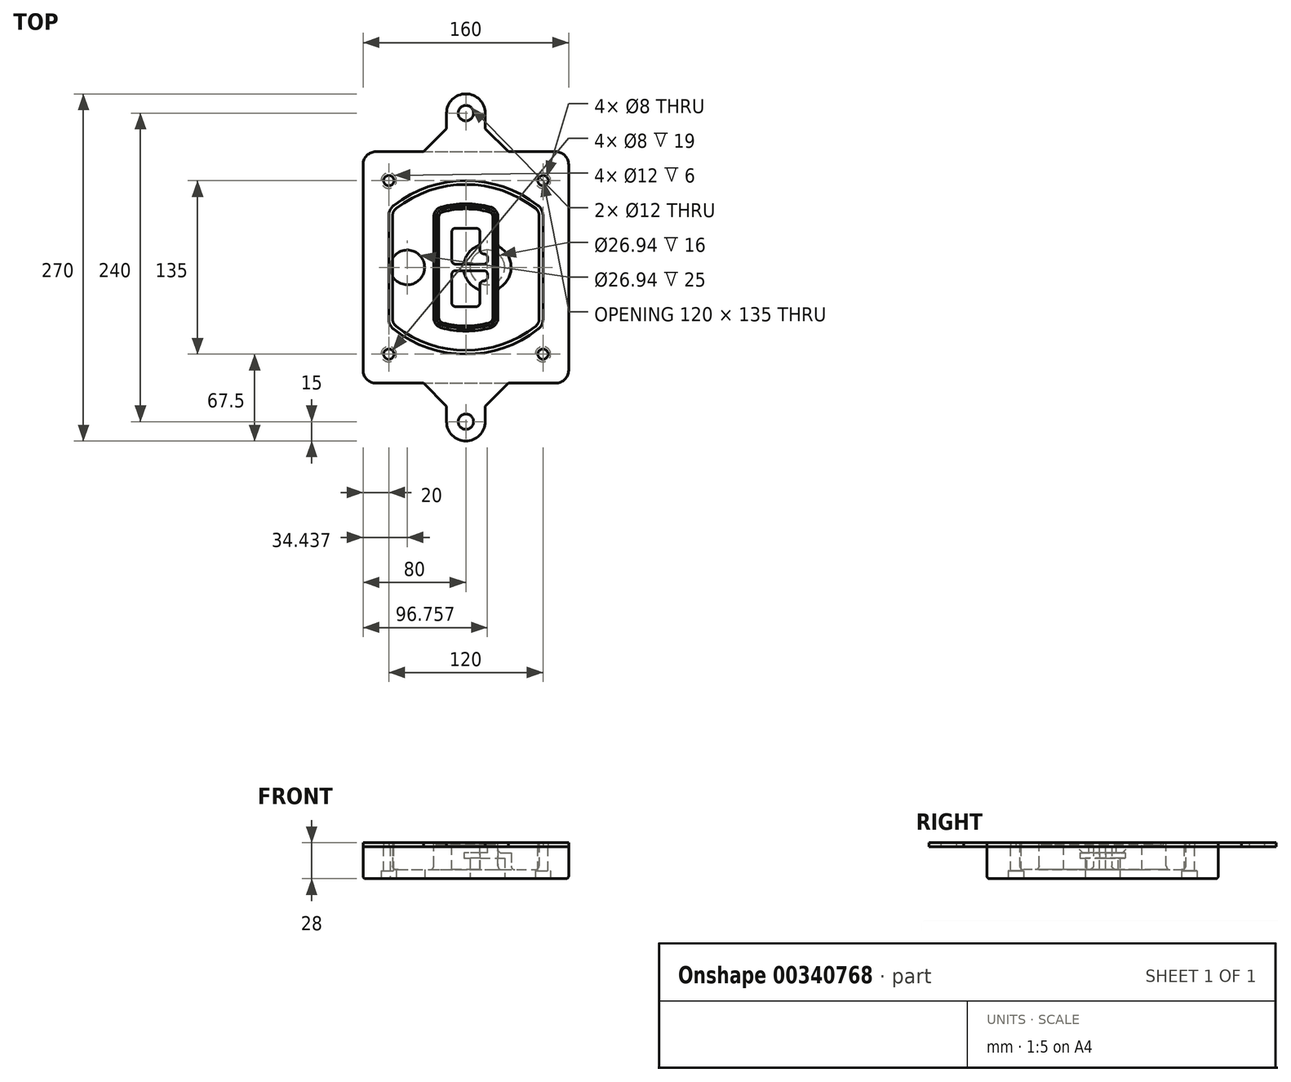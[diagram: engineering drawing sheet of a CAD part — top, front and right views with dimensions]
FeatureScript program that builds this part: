
annotation { "Feature Type Name" : "Feature", "Feature Type Description" : "" }
export const myFeature = defineFeature(function(context is Context, id is Id, definition is map)
    precondition{}
    {
        {
            var Q0;
            Q0=qCreatedBy(makeId("Top.planeOp"),FACE);
            var sketch = newSketch(context, id + "F0", { "sketchPlane" : qUnion([Q0])});
            skPoint(sketch, "E0.rect.middle", {"position": v(0, 0) * mm});
            skLineSegment(sketch, "E1.bottom", {"start": v(-70, -90) * mm, "end": v(70, -90) * mm});
            skLineSegment(sketch, "E1.top", {"start": v(-70, 90) * mm, "end": v(70, 90) * mm});
            skLineSegment(sketch, "E1.left", {"start": v(-80, -80) * mm, "end": v(-80, 80) * mm});
            skLineSegment(sketch, "E1.right", {"start": v(80, -80) * mm, "end": v(80, 80) * mm});
            skLineSegment(sketch, "E2", {"start": v(-80, 90) * mm, "end": v(80, -90) * mm, "construction": true});
            skLineSegment(sketch, "E3", {"start": v(80, 90) * mm, "end": v(-80, -90) * mm, "construction": true});
            skCircle(sketch, "E4", {"center": v(-60, 67.5) * mm, "radius": 4 * mm});
            skCircle(sketch, "E5", {"center": v(60, 67.5) * mm, "radius": 4 * mm});
            skCircle(sketch, "E6", {"center": v(60, -67.5) * mm, "radius": 4 * mm});
            skCircle(sketch, "E7", {"center": v(-60, -67.5) * mm, "radius": 4 * mm});
            skLineSegment(sketch, "E8", {"start": v(-60, 67.5) * mm, "end": v(60, 67.5) * mm, "construction": true});
            skLineSegment(sketch, "E9", {"start": v(60, 67.5) * mm, "end": v(60, -67.5) * mm, "construction": true});
            skLineSegment(sketch, "E10", {"start": v(60, -67.5) * mm, "end": v(-60, -67.5) * mm, "construction": true});
            skLineSegment(sketch, "E11", {"start": v(-60, -67.5) * mm, "end": v(-60, 67.5) * mm, "construction": true});
            skLineSegment(sketch, "E12", {"start": v(-60, 40.3) * mm, "end": v(-60, -40.3) * mm});
            skLineSegment(sketch, "E13", {"start": v(60, 40.3) * mm, "end": v(60, -40.3) * mm});
            skArc(sketch, "E14", {"start": v(56.15, 48.18) * mm, "mid": v(0, 67.5) * mm, "end": v(-56.15, 48.18) * mm});
            skArc(sketch, "E15", {"start": v(-56.15, -48.18) * mm, "mid": v(0, -67.5) * mm, "end": v(56.15, -48.18) * mm});
            skLineSegment(sketch, "E16", {"start": v(-60, 0) * mm, "end": v(60, 0) * mm, "construction": true});
            skPoint(sketch, "E17.visualSharp", {"position": v(-60, -45) * mm});
            skArc(sketch, "E17.filletArc", {"start": v(-60, -40.3) * mm, "mid": v(-58.99, -44.68) * mm, "end": v(-56.15, -48.18) * mm});
            skPoint(sketch, "E18.visualSharp", {"position": v(-60, 45) * mm});
            skArc(sketch, "E18.filletArc", {"start": v(-56.15, 48.18) * mm, "mid": v(-58.99, 44.68) * mm, "end": v(-60, 40.3) * mm});
            skPoint(sketch, "E19.visualSharp", {"position": v(60, 45) * mm});
            skArc(sketch, "E19.filletArc", {"start": v(60, 40.3) * mm, "mid": v(58.99, 44.68) * mm, "end": v(56.15, 48.18) * mm});
            skPoint(sketch, "E20.visualSharp", {"position": v(60, -45) * mm});
            skArc(sketch, "E20.filletArc", {"start": v(56.15, -48.18) * mm, "mid": v(58.99, -44.68) * mm, "end": v(60, -40.3) * mm});
            skPoint(sketch, "E21.visualSharp", {"position": v(-80, 90) * mm});
            skArc(sketch, "E21.filletArc", {"start": v(-70, 90) * mm, "mid": v(-77.07, 87.07) * mm, "end": v(-80, 80) * mm});
            skPoint(sketch, "E22.visualSharp", {"position": v(80, 90) * mm});
            skArc(sketch, "E22.filletArc", {"start": v(80, 80) * mm, "mid": v(77.07, 87.07) * mm, "end": v(70, 90) * mm});
            skPoint(sketch, "E23.visualSharp", {"position": v(80, -90) * mm});
            skArc(sketch, "E23.filletArc", {"start": v(70, -90) * mm, "mid": v(77.07, -87.07) * mm, "end": v(80, -80) * mm});
            skPoint(sketch, "E24.visualSharp", {"position": v(-80, -90) * mm});
            skArc(sketch, "E24.filletArc", {"start": v(-80, -80) * mm, "mid": v(-77.07, -87.07) * mm, "end": v(-70, -90) * mm});
            skArc(sketch, "E25.0", {"start": v(57, 40.3) * mm, "mid": v(56.3, 43.36) * mm, "end": v(54.3, 45.81) * mm});
            skLineSegment(sketch, "E25.1", {"start": v(57, 40.3) * mm, "end": v(57, -40.3) * mm});
            skArc(sketch, "E25.2", {"start": v(54.3, -45.81) * mm, "mid": v(56.3, -43.36) * mm, "end": v(57, -40.3) * mm});
            skArc(sketch, "E25.3", {"start": v(-54.3, -45.81) * mm, "mid": v(0, -64.5) * mm, "end": v(54.3, -45.81) * mm});
            skArc(sketch, "E25.4", {"start": v(-57, -40.3) * mm, "mid": v(-56.3, -43.36) * mm, "end": v(-54.3, -45.81) * mm});
            skArc(sketch, "E25.5", {"start": v(54.3, 45.81) * mm, "mid": v(0, 64.5) * mm, "end": v(-54.3, 45.81) * mm});
            skLineSegment(sketch, "E25.6", {"start": v(-57, 40.3) * mm, "end": v(-57, -40.3) * mm});
            skArc(sketch, "E25.7", {"start": v(-54.3, 45.81) * mm, "mid": v(-56.3, 43.36) * mm, "end": v(-57, 40.3) * mm});
            skArc(sketch, "E26.0", {"start": v(-58.62, 51.33) * mm, "mid": v(-62.58, 46.43) * mm, "end": v(-64, 40.3) * mm});
            skArc(sketch, "E26.1", {"start": v(58.62, 51.33) * mm, "mid": v(0, 71.5) * mm, "end": v(-58.62, 51.33) * mm});
            skArc(sketch, "E26.2", {"start": v(64, 40.3) * mm, "mid": v(62.58, 46.43) * mm, "end": v(58.62, 51.33) * mm});
            skLineSegment(sketch, "E26.3", {"start": v(64, 40.3) * mm, "end": v(64, -40.3) * mm});
            skArc(sketch, "E26.4", {"start": v(58.62, -51.33) * mm, "mid": v(62.58, -46.43) * mm, "end": v(64, -40.3) * mm});
            skLineSegment(sketch, "E26.5", {"start": v(-64, 40.3) * mm, "end": v(-64, -40.3) * mm});
            skArc(sketch, "E26.6", {"start": v(-58.62, -51.33) * mm, "mid": v(0, -71.5) * mm, "end": v(58.62, -51.33) * mm});
            skArc(sketch, "E26.7", {"start": v(-64, -40.3) * mm, "mid": v(-62.58, -46.43) * mm, "end": v(-58.62, -51.33) * mm});
            skSolve(sketch);
        }
        {
            var Q0;
            Q0=makeQuery(id+"F0.imprint","IMPRINT",FACE,{"disambiguationData":[TD([[makeQuery(id+"F0.imprint","IMPRINT",EDGE,{"derivedFrom":sQuery(id+"F0.wireOp",EDGE,"E1.bottom")}),1.0]])]});
            var Q1;
            Q1=makeQuery(id+"F0.imprint","IMPRINT",FACE,{"disambiguationData":[TD([[makeQuery(id+"F0.imprint","IMPRINT",EDGE,{"derivedFrom":sQuery(id+"F0.wireOp",EDGE,"E12")}),1.0]])]});
            var Q2;
            Q2=makeQuery(id+"F0.imprint","IMPRINT",FACE,{"disambiguationData":[TD([[makeQuery(id+"F0.imprint","IMPRINT",EDGE,{"derivedFrom":sQuery(id+"F0.wireOp",EDGE,"E25.0")}),1.0]])]});
            var Q3;
            Q3=makeQuery(id+"F0.imprint","IMPRINT",FACE,{"disambiguationData":[TD([[makeQuery(id+"F0.imprint","IMPRINT",EDGE,{"derivedFrom":sQuery(id+"F0.wireOp",EDGE,"E12")}),-1.0]])]});
            extrude(context, id + "F1", {"entities" : qUnion([Q0, Q1, Q2, Q3]), "oppositeDirection" : true, "depth" : 25 * mm});
        }
        {
            var Q0;
            Q0=makeQuery(id+"F0.imprint","IMPRINT",FACE,{"disambiguationData":[TD([[makeQuery(id+"F0.imprint","IMPRINT",EDGE,{"derivedFrom":sQuery(id+"F0.wireOp",EDGE,"E12")}),1.0]])]});
            extrude(context, id + "F2", {"entities" : qUnion([Q0]), "operationType" : NewBodyOperationType.ADD, "depth" : 3 * mm});
        }
        {
            var Q0;
            Q0=makeQuery(id+"F0.imprint","IMPRINT",FACE,{"disambiguationData":[TD([[makeQuery(id+"F0.imprint","IMPRINT",EDGE,{"derivedFrom":sQuery(id+"F0.wireOp",EDGE,"E25.0")}),1.0]])]});
            extrude(context, id + "F3", {"entities" : qUnion([Q0]), "operationType" : NewBodyOperationType.REMOVE, "oppositeDirection" : true, "depth" : 18 * mm});
        }
        {
            var Q0;
            Q0=makeQuery(id+"F2.opExtrude","CAP_FACE",FACE,{"disambiguationData":[OSD([sQuery(id+"F0.wireOp",EDGE,"E12"),sQuery(id+"F0.wireOp",EDGE,"E13"),sQuery(id+"F0.wireOp",EDGE,"E14"),sQuery(id+"F0.wireOp",EDGE,"E15"),sQuery(id+"F0.wireOp",EDGE,"E17.filletArc"),sQuery(id+"F0.wireOp",EDGE,"E18.filletArc"),sQuery(id+"F0.wireOp",EDGE,"E19.filletArc"),sQuery(id+"F0.wireOp",EDGE,"E20.filletArc"),sQuery(id+"F0.wireOp",EDGE,"E25.0"),sQuery(id+"F0.wireOp",EDGE,"E25.1"),sQuery(id+"F0.wireOp",EDGE,"E25.2"),sQuery(id+"F0.wireOp",EDGE,"E25.3"),sQuery(id+"F0.wireOp",EDGE,"E25.4"),sQuery(id+"F0.wireOp",EDGE,"E25.5"),sQuery(id+"F0.wireOp",EDGE,"E25.6"),sQuery(id+"F0.wireOp",EDGE,"E25.7")])],"isStart":false});
            var sketch = newSketch(context, id + "F4", { "sketchPlane" : qUnion([Q0])});
            skArc(sketch, "E27.0", {"start": v(-19.08, -46.97) * mm, "mid": v(0, -49.5) * mm, "end": v(19.08, -46.97) * mm});
            skArc(sketch, "E28.0", {"start": v(19.08, 46.97) * mm, "mid": v(0, 49.5) * mm, "end": v(-19.08, 46.97) * mm});
            skLineSegment(sketch, "E29", {"start": v(-25, 39.25) * mm, "end": v(-25, -39.25) * mm});
            skLineSegment(sketch, "E30", {"start": v(25, 39.25) * mm, "end": v(25, -39.25) * mm});
            skLineSegment(sketch, "E31", {"start": v(-25, 45.1) * mm, "end": v(25, 45.1) * mm, "construction": true});
            skLineSegment(sketch, "E32", {"start": v(-25, -45.1) * mm, "end": v(25, -45.1) * mm, "construction": true});
            skPoint(sketch, "E33.visualSharp", {"position": v(-25, 45.1) * mm});
            skArc(sketch, "E33.filletArc", {"start": v(-19.08, 46.97) * mm, "mid": v(-23.35, 44.11) * mm, "end": v(-25, 39.25) * mm});
            skPoint(sketch, "E34.visualSharp", {"position": v(25, 45.1) * mm});
            skArc(sketch, "E34.filletArc", {"start": v(25, 39.25) * mm, "mid": v(23.35, 44.11) * mm, "end": v(19.08, 46.97) * mm});
            skPoint(sketch, "E35.visualSharp", {"position": v(25, -45.1) * mm});
            skArc(sketch, "E35.filletArc", {"start": v(19.08, -46.97) * mm, "mid": v(23.35, -44.11) * mm, "end": v(25, -39.25) * mm});
            skPoint(sketch, "E36.visualSharp", {"position": v(-25, -45.1) * mm});
            skArc(sketch, "E36.filletArc", {"start": v(-25, -39.25) * mm, "mid": v(-23.35, -44.11) * mm, "end": v(-19.08, -46.97) * mm});
            skArc(sketch, "E37.0", {"start": v(54.3, 45.81) * mm, "mid": v(0, 64.5) * mm, "end": v(-54.3, 45.81) * mm});
            skArc(sketch, "E37.1", {"start": v(-54.3, 45.81) * mm, "mid": v(-56.3, 43.36) * mm, "end": v(-57, 40.3) * mm});
            skLineSegment(sketch, "E37.2", {"start": v(-57, 40.3) * mm, "end": v(-57, -40.3) * mm});
            skArc(sketch, "E37.3", {"start": v(-57, -40.3) * mm, "mid": v(-56.3, -43.36) * mm, "end": v(-54.3, -45.81) * mm});
            skArc(sketch, "E37.4", {"start": v(-54.3, -45.81) * mm, "mid": v(0, -64.5) * mm, "end": v(54.3, -45.81) * mm});
            skArc(sketch, "E37.5", {"start": v(54.3, -45.81) * mm, "mid": v(56.3, -43.36) * mm, "end": v(57, -40.3) * mm});
            skLineSegment(sketch, "E37.6", {"start": v(57, 40.3) * mm, "end": v(57, -40.3) * mm});
            skArc(sketch, "E37.7", {"start": v(57, 40.3) * mm, "mid": v(56.3, 43.36) * mm, "end": v(54.3, 45.81) * mm});
            skLineSegment(sketch, "E38.0", {"start": v(23, 39.25) * mm, "end": v(23, -39.25) * mm});
            skArc(sketch, "E38.1", {"start": v(18.56, -45.04) * mm, "mid": v(21.76, -42.9) * mm, "end": v(23, -39.25) * mm});
            skArc(sketch, "E38.2", {"start": v(-18.56, -45.04) * mm, "mid": v(0, -47.5) * mm, "end": v(18.56, -45.04) * mm});
            skArc(sketch, "E38.3", {"start": v(-23, -39.25) * mm, "mid": v(-21.76, -42.9) * mm, "end": v(-18.56, -45.04) * mm});
            skLineSegment(sketch, "E38.4", {"start": v(-23, 39.25) * mm, "end": v(-23, -39.25) * mm});
            skArc(sketch, "E38.5", {"start": v(23, 39.25) * mm, "mid": v(21.76, 42.9) * mm, "end": v(18.56, 45.04) * mm});
            skArc(sketch, "E38.6", {"start": v(-18.56, 45.04) * mm, "mid": v(-21.76, 42.9) * mm, "end": v(-23, 39.25) * mm});
            skArc(sketch, "E38.7", {"start": v(18.56, 45.04) * mm, "mid": v(0, 47.5) * mm, "end": v(-18.56, 45.04) * mm});
            skArc(sketch, "E39.0", {"start": v(21, 39.25) * mm, "mid": v(20.18, 41.68) * mm, "end": v(18.04, 43.1) * mm});
            skLineSegment(sketch, "E39.1", {"start": v(21, 39.25) * mm, "end": v(21, -39.25) * mm});
            skArc(sketch, "E39.2", {"start": v(18.04, -43.1) * mm, "mid": v(20.18, -41.68) * mm, "end": v(21, -39.25) * mm});
            skArc(sketch, "E39.3", {"start": v(-18.04, -43.1) * mm, "mid": v(0, -45.5) * mm, "end": v(18.04, -43.1) * mm});
            skArc(sketch, "E39.4", {"start": v(-21, -39.25) * mm, "mid": v(-20.18, -41.68) * mm, "end": v(-18.04, -43.1) * mm});
            skArc(sketch, "E39.5", {"start": v(18.04, 43.1) * mm, "mid": v(0, 45.5) * mm, "end": v(-18.04, 43.1) * mm});
            skLineSegment(sketch, "E39.6", {"start": v(-21, 39.25) * mm, "end": v(-21, -39.25) * mm});
            skArc(sketch, "E39.7", {"start": v(-18.04, 43.1) * mm, "mid": v(-20.18, 41.68) * mm, "end": v(-21, 39.25) * mm});
            skLineSegment(sketch, "E40", {"start": v(-25, 0) * mm, "end": v(25, 0) * mm, "construction": true});
            skLineSegment(sketch, "E41", {"start": v(-11, 5.5) * mm, "end": v(-11, 27.5) * mm});
            skLineSegment(sketch, "E42", {"start": v(-8, 30.5) * mm, "end": v(8, 30.5) * mm});
            skLineSegment(sketch, "E43", {"start": v(11, 27.5) * mm, "end": v(11, 13.5) * mm});
            skLineSegment(sketch, "E44", {"start": v(14, 10.5) * mm, "end": v(14, 10.5) * mm});
            skLineSegment(sketch, "E45", {"start": v(17, 7.5) * mm, "end": v(17, 5.5) * mm});
            skLineSegment(sketch, "E46", {"start": v(14, 2.5) * mm, "end": v(-8, 2.5) * mm});
            skPoint(sketch, "E47.visualSharp", {"position": v(-11, 30.5) * mm});
            skArc(sketch, "E47.filletArc", {"start": v(-8, 30.5) * mm, "mid": v(-10.12, 29.62) * mm, "end": v(-11, 27.5) * mm});
            skPoint(sketch, "E48.visualSharp", {"position": v(11, 30.5) * mm});
            skArc(sketch, "E48.filletArc", {"start": v(11, 27.5) * mm, "mid": v(10.12, 29.62) * mm, "end": v(8, 30.5) * mm});
            skPoint(sketch, "E49.visualSharp", {"position": v(11, 10.5) * mm});
            skArc(sketch, "E49.filletArc", {"start": v(11, 13.5) * mm, "mid": v(11.88, 11.38) * mm, "end": v(14, 10.5) * mm});
            skPoint(sketch, "E50.visualSharp", {"position": v(17, 10.5) * mm});
            skArc(sketch, "E50.filletArc", {"start": v(17, 7.5) * mm, "mid": v(16.12, 9.62) * mm, "end": v(14, 10.5) * mm});
            skPoint(sketch, "E51.visualSharp", {"position": v(17, 2.5) * mm});
            skArc(sketch, "E51.filletArc", {"start": v(14, 2.5) * mm, "mid": v(16.12, 3.38) * mm, "end": v(17, 5.5) * mm});
            skPoint(sketch, "E52.visualSharp", {"position": v(-11, 2.5) * mm});
            skArc(sketch, "E52.filletArc", {"start": v(-11, 5.5) * mm, "mid": v(-10.12, 3.38) * mm, "end": v(-8, 2.5) * mm});
            skLineSegment(sketch, "E53.0.MirrorCS", {"start": v(14, -2.5) * mm, "end": v(-8, -2.5) * mm});
            skArc(sketch, "E54.0.MirrorCS", {"start": v(-11, -5.5) * mm, "mid": v(-10.12, -3.38) * mm, "end": v(-8, -2.5) * mm});
            skLineSegment(sketch, "E55.0.MirrorCS", {"start": v(-11, -5.5) * mm, "end": v(-11, -27.5) * mm});
            skArc(sketch, "E56.0.MirrorCS", {"start": v(-8, -30.5) * mm, "mid": v(-10.12, -29.62) * mm, "end": v(-11, -27.5) * mm});
            skLineSegment(sketch, "E57.0.MirrorCS", {"start": v(-8, -30.5) * mm, "end": v(8, -30.5) * mm});
            skArc(sketch, "E58.0.MirrorCS", {"start": v(11, -27.5) * mm, "mid": v(10.12, -29.62) * mm, "end": v(8, -30.5) * mm});
            skLineSegment(sketch, "E59.0.MirrorCS", {"start": v(11, -27.5) * mm, "end": v(11, -13.5) * mm});
            skArc(sketch, "E60.0.MirrorCS", {"start": v(11, -13.5) * mm, "mid": v(11.88, -11.38) * mm, "end": v(14, -10.5) * mm});
            skArc(sketch, "E61.0.MirrorCS", {"start": v(17, -7.5) * mm, "mid": v(16.12, -9.62) * mm, "end": v(14, -10.5) * mm});
            skLineSegment(sketch, "E62.0.MirrorCS", {"start": v(17, -7.5) * mm, "end": v(17, -5.5) * mm});
            skArc(sketch, "E63.0.MirrorCS", {"start": v(14, -2.5) * mm, "mid": v(16.12, -3.38) * mm, "end": v(17, -5.5) * mm});
            skSolve(sketch);
        }
        {
            var Q0;
            Q0=makeQuery(id+"F4.imprint","IMPRINT",FACE,{"disambiguationData":[TD([[makeQuery(id+"F4.imprint","IMPRINT",EDGE,{"derivedFrom":sQuery(id+"F4.wireOp",EDGE,"E27.0")}),1.0]])]});
            var Q1;
            Q1=makeQuery(id+"F4.imprint","IMPRINT",FACE,{"disambiguationData":[TD([[makeQuery(id+"F4.imprint","IMPRINT",EDGE,{"derivedFrom":sQuery(id+"F4.wireOp",EDGE,"E38.0")}),-1.0]])]});
            var Q2;
            Q2=makeQuery(id+"F4.imprint","IMPRINT",FACE,{"disambiguationData":[TD([[makeQuery(id+"F4.imprint","IMPRINT",EDGE,{"derivedFrom":sQuery(id+"F4.wireOp",EDGE,"E39.0")}),1.0]])]});
            extrude(context, id + "F5", {"entities" : qUnion([Q0, Q1, Q2]), "operationType" : NewBodyOperationType.ADD, "endBound" : BoundingType.UP_TO_NEXT, "oppositeDirection" : true, "depth" : 25 * mm});
        }
        {
            var Q0;
            Q0=makeQuery(id+"F4.imprint","IMPRINT",FACE,{"disambiguationData":[TD([[makeQuery(id+"F4.imprint","IMPRINT",EDGE,{"derivedFrom":sQuery(id+"F4.wireOp",EDGE,"E38.0")}),-1.0]])]});
            extrude(context, id + "F6", {"entities" : qUnion([Q0]), "operationType" : NewBodyOperationType.REMOVE, "oppositeDirection" : true, "depth" : 2 * mm});
        }
        {
            var Q0;
            Q0=makeQuery(id+"F1.opExtrude","CAP_FACE",FACE,{"disambiguationData":[OSD([sQuery(id+"F0.wireOp",EDGE,"E1.bottom"),sQuery(id+"F0.wireOp",EDGE,"E1.top"),sQuery(id+"F0.wireOp",EDGE,"E1.left"),sQuery(id+"F0.wireOp",EDGE,"E1.right"),sQuery(id+"F0.wireOp",EDGE,"E4"),sQuery(id+"F0.wireOp",EDGE,"E5"),sQuery(id+"F0.wireOp",EDGE,"E6"),sQuery(id+"F0.wireOp",EDGE,"E7"),sQuery(id+"F0.wireOp",EDGE,"E21.filletArc"),sQuery(id+"F0.wireOp",EDGE,"E22.filletArc"),sQuery(id+"F0.wireOp",EDGE,"E23.filletArc"),sQuery(id+"F0.wireOp",EDGE,"E24.filletArc")])],"isStart":false});
            var sketch = newSketch(context, id + "F7", { "sketchPlane" : qUnion([Q0])});
            skCircle(sketch, "E64", {"center": v(16.76, 0) * mm, "radius": 13.47 * mm});
            skCircle(sketch, "E65", {"center": v(-45.56, 0) * mm, "radius": 13.47 * mm});
            skLineSegment(sketch, "E66", {"start": v(80, 0) * mm, "end": v(-80, 0) * mm});
            skCircle(sketch, "E67", {"center": v(16.76, 0) * mm, "radius": 18.47 * mm});
            skCircle(sketch, "E68", {"center": v(60, -67.5) * mm, "radius": 6 * mm});
            skCircle(sketch, "E69", {"center": v(-60, -67.5) * mm, "radius": 6 * mm});
            skCircle(sketch, "E70", {"center": v(-60, 67.5) * mm, "radius": 6 * mm});
            skCircle(sketch, "E71", {"center": v(60, 67.5) * mm, "radius": 6 * mm});
            skSolve(sketch);
        }
        {
            var Q0;
            {var subQ1=sQuery(id+"F7.wireOp",EDGE,"E66");var subQ4=sQuery(id+"F7.wireOp",EDGE,"E64");var subQ6=makeQuery(id+"F7.imprint","INTERSECT",VERTEX,{"disambiguationData":[OD(0.0)],"derivedFrom":[subQ4,subQ1]});Q0=makeQuery(id+"F7.imprint","IMPRINT",FACE,{"disambiguationData":[TD([[makeQuery(id+"F7.imprint","IMPRINT",EDGE,{"disambiguationData":[TD([[subQ6,-1.0]])],"derivedFrom":subQ4}),-1.0]])]});}
            var Q1;
            {var subQ0=sQuery(id+"F7.wireOp",EDGE,"E66");var subQ1=sQuery(id+"F7.wireOp",EDGE,"E64");var subQ3=makeQuery(id+"F7.imprint","INTERSECT",VERTEX,{"disambiguationData":[OD(0.0)],"derivedFrom":[subQ1,subQ0]});Q1=makeQuery(id+"F7.imprint","IMPRINT",FACE,{"disambiguationData":[TD([[makeQuery(id+"F7.imprint","IMPRINT",EDGE,{"disambiguationData":[TD([[subQ3,-1.0]])],"derivedFrom":subQ1}),1.0]])]});}
            var Q2;
            {var subQ0=sQuery(id+"F7.wireOp",EDGE,"E66");var subQ1=sQuery(id+"F7.wireOp",EDGE,"E64");var subQ3=makeQuery(id+"F7.imprint","INTERSECT",VERTEX,{"disambiguationData":[OD(0.0)],"derivedFrom":[subQ1,subQ0]});Q2=makeQuery(id+"F7.imprint","IMPRINT",FACE,{"disambiguationData":[TD([[makeQuery(id+"F7.imprint","IMPRINT",EDGE,{"disambiguationData":[TD([[subQ3,1.0]])],"derivedFrom":subQ1}),1.0]])]});}
            var Q3;
            {var subQ1=sQuery(id+"F7.wireOp",EDGE,"E66");var subQ4=sQuery(id+"F7.wireOp",EDGE,"E64");var subQ6=makeQuery(id+"F7.imprint","INTERSECT",VERTEX,{"disambiguationData":[OD(0.0)],"derivedFrom":[subQ4,subQ1]});Q3=makeQuery(id+"F7.imprint","IMPRINT",FACE,{"disambiguationData":[TD([[makeQuery(id+"F7.imprint","IMPRINT",EDGE,{"disambiguationData":[TD([[subQ6,1.0]])],"derivedFrom":subQ4}),-1.0]])]});}
            extrude(context, id + "F8", {"entities" : qUnion([Q0, Q1, Q2, Q3]), "operationType" : NewBodyOperationType.ADD, "oppositeDirection" : true, "depth" : 20 * mm});
        }
        {
            var Q0;
            {var subQ0=sQuery(id+"F7.wireOp",EDGE,"E66");var subQ1=sQuery(id+"F7.wireOp",EDGE,"E64");var subQ3=makeQuery(id+"F7.imprint","INTERSECT",VERTEX,{"disambiguationData":[OD(0.0)],"derivedFrom":[subQ1,subQ0]});Q0=makeQuery(id+"F7.imprint","IMPRINT",FACE,{"disambiguationData":[TD([[makeQuery(id+"F7.imprint","IMPRINT",EDGE,{"disambiguationData":[TD([[subQ3,-1.0]])],"derivedFrom":subQ1}),1.0]])]});}
            var Q1;
            {var subQ0=sQuery(id+"F7.wireOp",EDGE,"E66");var subQ1=sQuery(id+"F7.wireOp",EDGE,"E64");var subQ3=makeQuery(id+"F7.imprint","INTERSECT",VERTEX,{"disambiguationData":[OD(0.0)],"derivedFrom":[subQ1,subQ0]});Q1=makeQuery(id+"F7.imprint","IMPRINT",FACE,{"disambiguationData":[TD([[makeQuery(id+"F7.imprint","IMPRINT",EDGE,{"disambiguationData":[TD([[subQ3,1.0]])],"derivedFrom":subQ1}),1.0]])]});}
            extrude(context, id + "F9", {"entities" : qUnion([Q0, Q1]), "operationType" : NewBodyOperationType.REMOVE, "oppositeDirection" : true, "depth" : 16 * mm});
        }
        {
            var Q0;
            {var subQ0=sQuery(id+"F7.wireOp",EDGE,"E66");var subQ1=sQuery(id+"F7.wireOp",EDGE,"E65");var subQ3=makeQuery(id+"F7.imprint","INTERSECT",VERTEX,{"disambiguationData":[OD(0.0)],"derivedFrom":[subQ1,subQ0]});Q0=makeQuery(id+"F7.imprint","IMPRINT",FACE,{"disambiguationData":[TD([[makeQuery(id+"F7.imprint","IMPRINT",EDGE,{"disambiguationData":[TD([[subQ3,-1.0]])],"derivedFrom":subQ1}),1.0]])]});}
            var Q1;
            {var subQ0=sQuery(id+"F7.wireOp",EDGE,"E66");var subQ1=sQuery(id+"F7.wireOp",EDGE,"E65");var subQ3=makeQuery(id+"F7.imprint","INTERSECT",VERTEX,{"disambiguationData":[OD(0.0)],"derivedFrom":[subQ1,subQ0]});Q1=makeQuery(id+"F7.imprint","IMPRINT",FACE,{"disambiguationData":[TD([[makeQuery(id+"F7.imprint","IMPRINT",EDGE,{"disambiguationData":[TD([[subQ3,1.0]])],"derivedFrom":subQ1}),1.0]])]});}
            extrude(context, id + "F10", {"entities" : qUnion([Q0, Q1]), "operationType" : NewBodyOperationType.REMOVE, "oppositeDirection" : true, "depth" : 25 * mm});
        }
        {
            var Q0;
            Q0=makeQuery(id+"F7.imprint","IMPRINT",FACE,{"disambiguationData":[TD([[makeQuery(id+"F7.imprint","IMPRINT",EDGE,{"derivedFrom":sQuery(id+"F7.wireOp",EDGE,"E68")}),1.0]])]});
            var Q1;
            Q1=makeQuery(id+"F7.imprint","IMPRINT",FACE,{"disambiguationData":[TD([[makeQuery(id+"F7.imprint","IMPRINT",EDGE,{"derivedFrom":makeQuery(id+"F1.opExtrude","CAP_EDGE",EDGE,{"disambiguationData":[OSD([sQuery(id+"F0.wireOp",EDGE,"E5")])],"isStart":false})}),-1.0]])]});
            var Q2;
            Q2=makeQuery(id+"F7.imprint","IMPRINT",FACE,{"disambiguationData":[TD([[makeQuery(id+"F7.imprint","IMPRINT",EDGE,{"derivedFrom":sQuery(id+"F7.wireOp",EDGE,"E69")}),1.0]])]});
            var Q3;
            Q3=makeQuery(id+"F7.imprint","IMPRINT",FACE,{"disambiguationData":[TD([[makeQuery(id+"F7.imprint","IMPRINT",EDGE,{"derivedFrom":makeQuery(id+"F1.opExtrude","CAP_EDGE",EDGE,{"disambiguationData":[OSD([sQuery(id+"F0.wireOp",EDGE,"E4")])],"isStart":false})}),-1.0]])]});
            var Q4;
            Q4=makeQuery(id+"F7.imprint","IMPRINT",FACE,{"disambiguationData":[TD([[makeQuery(id+"F7.imprint","IMPRINT",EDGE,{"derivedFrom":sQuery(id+"F7.wireOp",EDGE,"E70")}),1.0]])]});
            var Q5;
            Q5=makeQuery(id+"F7.imprint","IMPRINT",FACE,{"disambiguationData":[TD([[makeQuery(id+"F7.imprint","IMPRINT",EDGE,{"derivedFrom":makeQuery(id+"F1.opExtrude","CAP_EDGE",EDGE,{"disambiguationData":[OSD([sQuery(id+"F0.wireOp",EDGE,"E7")])],"isStart":false})}),-1.0]])]});
            var Q6;
            Q6=makeQuery(id+"F7.imprint","IMPRINT",FACE,{"disambiguationData":[TD([[makeQuery(id+"F7.imprint","IMPRINT",EDGE,{"derivedFrom":sQuery(id+"F7.wireOp",EDGE,"E71")}),1.0]])]});
            var Q7;
            Q7=makeQuery(id+"F7.imprint","IMPRINT",FACE,{"disambiguationData":[TD([[makeQuery(id+"F7.imprint","IMPRINT",EDGE,{"derivedFrom":makeQuery(id+"F1.opExtrude","CAP_EDGE",EDGE,{"disambiguationData":[OSD([sQuery(id+"F0.wireOp",EDGE,"E6")])],"isStart":false})}),-1.0]])]});
            extrude(context, id + "F11", {"entities" : qUnion([Q0, Q1, Q2, Q3, Q4, Q5, Q6, Q7]), "operationType" : NewBodyOperationType.REMOVE, "oppositeDirection" : true, "depth" : 6 * mm});
        }
        {
            var Q0;
            Q0=makeQuery(id+"F9.boolean.opBoolean","COPY",FACE,{"derivedFrom":makeQuery(id+"F9.opExtrude","CAP_FACE",FACE,{"disambiguationData":[OSD([sQuery(id+"F7.wireOp",EDGE,"E64")])],"isStart":false})});
            var sketch = newSketch(context, id + "F12", { "sketchPlane" : qUnion([Q0])});
            skArc(sketch, "E72.0", {"start": v(11, 17.55) * mm, "mid": v(2.57, 11.82) * mm, "end": v(-1.54, 2.5) * mm});
            skArc(sketch, "E72.1", {"start": v(-1.54, -2.5) * mm, "mid": v(2.57, -11.82) * mm, "end": v(11, -17.55) * mm});
            skLineSegment(sketch, "E73", {"start": v(-1.54, -2.5) * mm, "end": v(14, -2.5) * mm});
            skLineSegment(sketch, "E74.0", {"start": v(14, 2.5) * mm, "end": v(-1.54, 2.5) * mm});
            skArc(sketch, "E74.1", {"start": v(14, 2.5) * mm, "mid": v(16.12, 3.38) * mm, "end": v(17, 5.5) * mm});
            skLineSegment(sketch, "E74.2", {"start": v(17, 7.5) * mm, "end": v(17, 5.5) * mm});
            skArc(sketch, "E74.3", {"start": v(17, 7.5) * mm, "mid": v(16.12, 9.62) * mm, "end": v(14, 10.5) * mm});
            skArc(sketch, "E74.4", {"start": v(11, 13.5) * mm, "mid": v(11.88, 11.38) * mm, "end": v(14, 10.5) * mm});
            skLineSegment(sketch, "E74.5", {"start": v(11, 17.55) * mm, "end": v(11, 13.5) * mm});
            skLineSegment(sketch, "E74.7", {"start": v(14, -2.5) * mm, "end": v(-1.54, -2.5) * mm});
            skArc(sketch, "E74.8", {"start": v(14, -2.5) * mm, "mid": v(16.12, -3.38) * mm, "end": v(17, -5.5) * mm});
            skLineSegment(sketch, "E74.9", {"start": v(17, -7.5) * mm, "end": v(17, -5.5) * mm});
            skArc(sketch, "E74.10", {"start": v(17, -7.5) * mm, "mid": v(16.12, -9.62) * mm, "end": v(14, -10.5) * mm});
            skArc(sketch, "E74.11", {"start": v(11, -13.5) * mm, "mid": v(11.88, -11.38) * mm, "end": v(14, -10.5) * mm});
            skLineSegment(sketch, "E74.12", {"start": v(11, -17.55) * mm, "end": v(11, -13.5) * mm});
            skPoint(sketch, "E75.orphan", {"position": v(11, -27.5) * mm});
            skPoint(sketch, "E76.orphan", {"position": v(-8, -2.5) * mm});
            skPoint(sketch, "E77.orphan", {"position": v(-8, 2.5) * mm});
            skPoint(sketch, "E78.orphan", {"position": v(11, 27.5) * mm});
            skSolve(sketch);
        }
        {
            var Q0;
            {var subQ7=sQuery(id+"F12.wireOp",EDGE,"E72.0");var subQ14=sQuery(id+"F12.wireOp",EDGE,"E72.1");var subQ16=sQuery(id+"F12.wireOp",EDGE,"E74.1");var subQ18=sQuery(id+"F12.wireOp",EDGE,"E74.8");Q0=qUnion([makeQuery(id+"F12.imprint","IMPRINT",FACE,{"disambiguationData":[TD([[makeQuery(id+"F12.imprint","IMPRINT",EDGE,{"derivedFrom":subQ7}),1.0]])]}),makeQuery(id+"F12.imprint","IMPRINT",FACE,{"disambiguationData":[TD([[makeQuery(id+"F12.imprint","IMPRINT",EDGE,{"derivedFrom":subQ14}),1.0]])]}),makeQuery(id+"F12.imprint","IMPRINT",FACE,{"disambiguationData":[TD([[makeQuery(id+"F12.imprint","IMPRINT",EDGE,{"derivedFrom":subQ16}),1.0]])]}),makeQuery(id+"F12.imprint","IMPRINT",FACE,{"disambiguationData":[TD([[makeQuery(id+"F12.imprint","IMPRINT",EDGE,{"derivedFrom":subQ18}),-1.0]])]})]);}
            var Q1;
            Q1=makeQuery(id+"F5.boolean.opBoolean","SPLIT",FACE,{"disambiguationData":[TD([makeQuery(id+"F5.opExtrude","SWEPT_FACE",FACE,{"disambiguationData":[OSD([sQuery(id+"F4.wireOp",EDGE,"E41")])]})])],"derivedFrom":makeQuery(id+"F3.boolean.opBoolean","COPY",FACE,{"derivedFrom":makeQuery(id+"F3.opExtrude","CAP_FACE",FACE,{"disambiguationData":[OSD([sQuery(id+"F0.wireOp",EDGE,"E25.0"),sQuery(id+"F0.wireOp",EDGE,"E25.1"),sQuery(id+"F0.wireOp",EDGE,"E25.2"),sQuery(id+"F0.wireOp",EDGE,"E25.3"),sQuery(id+"F0.wireOp",EDGE,"E25.4"),sQuery(id+"F0.wireOp",EDGE,"E25.5"),sQuery(id+"F0.wireOp",EDGE,"E25.6"),sQuery(id+"F0.wireOp",EDGE,"E25.7")])],"isStart":false})})});
            extrude(context, id + "F13", {"entities" : qUnion([Q0]), "operationType" : NewBodyOperationType.REMOVE, "endBound" : BoundingType.UP_TO_SURFACE, "endBoundEntityFace" : qUnion([Q1]), "depth" : 25 * mm});
        }
        {
            var Q0;
            Q0=makeQuery(id+"F3.boolean.opBoolean","COPY",EDGE,{"derivedFrom":makeQuery(id+"F3.opExtrude","CAP_EDGE",EDGE,{"disambiguationData":[OSD([sQuery(id+"F0.wireOp",EDGE,"E25.6")])],"isStart":false})});
            var Q1;
            Q1=makeQuery(id+"F8.boolean.opBoolean","INTERSECT",EDGE,{"derivedFrom":[makeQuery(id+"F5.opExtrude","SWEPT_FACE",FACE,{"disambiguationData":[OSD([sQuery(id+"F4.wireOp",EDGE,"E30")])]}),makeQuery(id+"F8.opExtrude","CAP_FACE",FACE,{"disambiguationData":[OSD([sQuery(id+"F7.wireOp",EDGE,"E67")])],"isStart":false})]});
            var Q2;
            Q2=makeQuery(id+"F8.boolean.opBoolean","INTERSECT",EDGE,{"disambiguationData":[OD(1.0)],"derivedFrom":[makeQuery(id+"F5.opExtrude","SWEPT_FACE",FACE,{"disambiguationData":[OSD([sQuery(id+"F4.wireOp",EDGE,"E30")])]}),makeQuery(id+"F8.opExtrude","SWEPT_FACE",FACE,{"disambiguationData":[OSD([sQuery(id+"F7.wireOp",EDGE,"E67")])]})]});
            var Q3;
            {var subQ0=sQuery(id+"F4.wireOp",EDGE,"E30");Q3=makeQuery(id+"F8.boolean.opBoolean","SPLIT",EDGE,{"disambiguationData":[TD([makeQuery(id+"F5.opExtrude","SWEPT_FACE",FACE,{"disambiguationData":[OSD([sQuery(id+"F4.wireOp",EDGE,"E35.filletArc")])]})])],"derivedFrom":makeQuery(id+"F5.opExtrude","CAP_EDGE",EDGE,{"disambiguationData":[OSD([subQ0])],"isStart":false})});}
            var Q4;
            {var subQ0=sQuery(id+"F0.wireOp",EDGE,"E25.7");var subQ1=sQuery(id+"F0.wireOp",EDGE,"E25.1");var subQ2=sQuery(id+"F0.wireOp",EDGE,"E25.6");var subQ3=sQuery(id+"F0.wireOp",EDGE,"E25.5");var subQ4=sQuery(id+"F0.wireOp",EDGE,"E25.4");var subQ5=sQuery(id+"F0.wireOp",EDGE,"E25.0");var subQ6=sQuery(id+"F0.wireOp",EDGE,"E25.2");var subQ7=sQuery(id+"F0.wireOp",EDGE,"E25.3");Q4=makeQuery(id+"F8.boolean.opBoolean","INTERSECT",EDGE,{"derivedFrom":[makeQuery(id+"F5.boolean.opBoolean","SPLIT",FACE,{"disambiguationData":[TD([makeQuery(id+"F2.opExtrude","SWEPT_FACE",FACE,{"disambiguationData":[OSD([subQ5])]})])],"derivedFrom":makeQuery(id+"F3.boolean.opBoolean","COPY",FACE,{"derivedFrom":makeQuery(id+"F3.opExtrude","CAP_FACE",FACE,{"disambiguationData":[OSD([subQ5,subQ1,subQ6,subQ7,subQ4,subQ3,subQ2,subQ0])],"isStart":false})})}),makeQuery(id+"F8.opExtrude","SWEPT_FACE",FACE,{"disambiguationData":[OSD([sQuery(id+"F7.wireOp",EDGE,"E67")])]})]});}
            var Q5;
            Q5=makeQuery(id+"F8.boolean.opBoolean","INTERSECT",EDGE,{"disambiguationData":[OD(0.0)],"derivedFrom":[makeQuery(id+"F5.opExtrude","SWEPT_FACE",FACE,{"disambiguationData":[OSD([sQuery(id+"F4.wireOp",EDGE,"E30")])]}),makeQuery(id+"F8.opExtrude","SWEPT_FACE",FACE,{"disambiguationData":[OSD([sQuery(id+"F7.wireOp",EDGE,"E67")])]})]});
            fillet(context, id + "F14", {"entities" : qUnion([Q0, Q1, Q2, Q3, Q4, Q5]), "radius" : 3 * mm, "tangentPropagation" : true, "allowEdgeOverflow" : false});
        }
        {
            var Q0;
            Q0=makeQuery(id+"F1.opExtrude","CAP_EDGE",EDGE,{"disambiguationData":[OSD([sQuery(id+"F0.wireOp",EDGE,"E1.bottom")])],"isStart":false});
            fillet(context, id + "F15", {"entities" : qUnion([Q0]), "radius" : 2 * mm, "tangentPropagation" : true, "allowEdgeOverflow" : false});
        }
        {
            var Q0;
            {var subQ0=sQuery(id+"F0.wireOp",EDGE,"E21.filletArc");var subQ1=sQuery(id+"F0.wireOp",EDGE,"E7");var subQ2=sQuery(id+"F0.wireOp",EDGE,"E6");var subQ3=sQuery(id+"F0.wireOp",EDGE,"E5");var subQ4=sQuery(id+"F0.wireOp",EDGE,"E4");var subQ5=sQuery(id+"F0.wireOp",EDGE,"E22.filletArc");var subQ6=sQuery(id+"F0.wireOp",EDGE,"E1.bottom");var subQ7=sQuery(id+"F0.wireOp",EDGE,"E1.right");var subQ8=sQuery(id+"F0.wireOp",EDGE,"E1.top");var subQ9=sQuery(id+"F0.wireOp",EDGE,"E1.left");var subQ10=sQuery(id+"F0.wireOp",EDGE,"E23.filletArc");var subQ11=sQuery(id+"F0.wireOp",EDGE,"E24.filletArc");Q0=makeQuery(id+"F2.boolean.opBoolean","SPLIT",FACE,{"disambiguationData":[TD([makeQuery(id+"F1.opExtrude","SWEPT_FACE",FACE,{"disambiguationData":[OSD([subQ6])]})])],"derivedFrom":makeQuery(id+"F1.opExtrude","CAP_FACE",FACE,{"disambiguationData":[OSD([subQ6,subQ8,subQ9,subQ7,subQ4,subQ3,subQ2,subQ1,subQ0,subQ5,subQ10,subQ11])],"isStart":true})});}
            var sketch = newSketch(context, id + "F16", { "sketchPlane" : qUnion([Q0])});
            skLineSegment(sketch, "E79.0", {"start": v(80, -80) * mm, "end": v(80, 80) * mm});
            skArc(sketch, "E79.1", {"start": v(80, 80) * mm, "mid": v(77.07, 87.07) * mm, "end": v(70, 90) * mm});
            skLineSegment(sketch, "E79.2", {"start": v(-70, 90) * mm, "end": v(70, 90) * mm});
            skArc(sketch, "E79.3", {"start": v(-70, 90) * mm, "mid": v(-77.07, 87.07) * mm, "end": v(-80, 80) * mm});
            skLineSegment(sketch, "E79.4", {"start": v(-80, -80) * mm, "end": v(-80, 80) * mm});
            skArc(sketch, "E79.5", {"start": v(-80, -80) * mm, "mid": v(-77.07, -87.07) * mm, "end": v(-70, -90) * mm});
            skLineSegment(sketch, "E79.6", {"start": v(-70, -90) * mm, "end": v(70, -90) * mm});
            skArc(sketch, "E79.7", {"start": v(70, -90) * mm, "mid": v(77.07, -87.07) * mm, "end": v(80, -80) * mm});
            skCircle(sketch, "E79.8", {"center": v(60, -67.5) * mm, "radius": 4 * mm});
            skArc(sketch, "E79.9", {"start": v(-56.15, -48.18) * mm, "mid": v(0, -67.5) * mm, "end": v(56.15, -48.18) * mm});
            skArc(sketch, "E79.10", {"start": v(56.15, -48.18) * mm, "mid": v(58.99, -44.68) * mm, "end": v(60, -40.3) * mm});
            skLineSegment(sketch, "E79.11", {"start": v(60, 40.3) * mm, "end": v(60, -40.3) * mm});
            skArc(sketch, "E79.12", {"start": v(60, 40.3) * mm, "mid": v(58.99, 44.68) * mm, "end": v(56.15, 48.18) * mm});
            skArc(sketch, "E79.13", {"start": v(56.15, 48.18) * mm, "mid": v(0, 67.5) * mm, "end": v(-56.15, 48.18) * mm});
            skLineSegment(sketch, "E79.14", {"start": v(-60, 40.3) * mm, "end": v(-60, -40.3) * mm});
            skArc(sketch, "E79.15", {"start": v(-56.15, 48.18) * mm, "mid": v(-58.99, 44.68) * mm, "end": v(-60, 40.3) * mm});
            skArc(sketch, "E79.16", {"start": v(-60, -40.3) * mm, "mid": v(-58.99, -44.68) * mm, "end": v(-56.15, -48.18) * mm});
            skCircle(sketch, "E79.17", {"center": v(-60, -67.5) * mm, "radius": 4 * mm});
            skCircle(sketch, "E79.18", {"center": v(-60, 67.5) * mm, "radius": 4 * mm});
            skCircle(sketch, "E79.19", {"center": v(60, 67.5) * mm, "radius": 4 * mm});
            skCircle(sketch, "E80", {"center": v(0, 120) * mm, "radius": 6 * mm});
            skLineSegment(sketch, "E81", {"start": v(0, 120) * mm, "end": v(0, 90) * mm, "construction": true});
            skLineSegment(sketch, "E82", {"start": v(-15, 120) * mm, "end": v(-15, 108) * mm});
            skArc(sketch, "E83", {"start": v(-15, 120) * mm, "mid": v(0, 135) * mm, "end": v(15, 120) * mm});
            skLineSegment(sketch, "E84", {"start": v(15, 120) * mm, "end": v(15, 108) * mm});
            skLineSegment(sketch, "E85", {"start": v(15, 108) * mm, "end": v(33, 90) * mm});
            skArc(sketch, "E86.MirrorCS", {"start": v(15, 120) * mm, "mid": v(0, 135) * mm, "end": v(-15, 120) * mm});
            skLineSegment(sketch, "E87.MirrorCS", {"start": v(15, 92.25) * mm, "end": v(33, 74.25) * mm});
            skLineSegment(sketch, "E88.MirrorCS", {"start": v(-15, 92.25) * mm, "end": v(-33, 74.25) * mm});
            skArc(sketch, "E89.MirrorCS", {"start": v(15, 104.25) * mm, "mid": v(0, 119.25) * mm, "end": v(-15, 104.25) * mm});
            skLineSegment(sketch, "E90.MirrorCS", {"start": v(-110.43, 187.68) * mm, "end": v(-128.43, 169.68) * mm});
            skPoint(sketch, "E91", {"position": v(0, -67.5) * mm});
            skArc(sketch, "E92.MirrorCS", {"start": v(-15, 104.25) * mm, "mid": v(0, 119.25) * mm, "end": v(15, 104.25) * mm});
            skLineSegment(sketch, "E93.MirrorCS", {"start": v(110.43, 187.68) * mm, "end": v(128.43, 169.68) * mm});
            skLineSegment(sketch, "E94.MirrorCS", {"start": v(-15, 108) * mm, "end": v(-33, 90) * mm});
            skLineSegment(sketch, "E95", {"start": v(80, 0) * mm, "end": v(-80, 0) * mm, "construction": true});
            skLineSegment(sketch, "E96.MirrorCS", {"start": v(-15, -120) * mm, "end": v(-15, -108) * mm});
            skLineSegment(sketch, "E97.MirrorCS", {"start": v(15, -120) * mm, "end": v(15, -108) * mm});
            skArc(sketch, "E98.MirrorCS", {"start": v(15, -104.25) * mm, "mid": v(0, -119.25) * mm, "end": v(-15, -104.25) * mm});
            skCircle(sketch, "E99.MirrorC", {"center": v(0, -120) * mm, "radius": 6 * mm});
            skArc(sketch, "E100.MirrorCS", {"start": v(15, -120) * mm, "mid": v(0, -135) * mm, "end": v(-15, -120) * mm});
            skArc(sketch, "E101.MirrorCS", {"start": v(-15, -120) * mm, "mid": v(0, -135) * mm, "end": v(15, -120) * mm});
            skArc(sketch, "E102.MirrorCS", {"start": v(-15, -104.25) * mm, "mid": v(0, -119.25) * mm, "end": v(15, -104.25) * mm});
            skLineSegment(sketch, "E103.MirrorCS", {"start": v(-15, -108) * mm, "end": v(-33, -90) * mm});
            skLineSegment(sketch, "E104.MirrorCS", {"start": v(-15, -92.25) * mm, "end": v(-33, -74.25) * mm});
            skLineSegment(sketch, "E105.MirrorCS", {"start": v(15, -108) * mm, "end": v(33, -90) * mm});
            skLineSegment(sketch, "E106.MirrorCS", {"start": v(15, -92.25) * mm, "end": v(33, -74.25) * mm});
            skLineSegment(sketch, "E107.MirrorCS", {"start": v(110.43, -187.68) * mm, "end": v(128.43, -169.68) * mm});
            skLineSegment(sketch, "E108.MirrorCS", {"start": v(0, -120) * mm, "end": v(0, -90) * mm, "construction": true});
            skSolve(sketch);
        }
        {
            var Q0;
            Q0 = qSketchRegion(id + "F16", true);
            var Q1;
            Q1=makeQuery(id+"F2.opExtrude","CAP_FACE",FACE,{"disambiguationData":[OSD([sQuery(id+"F0.wireOp",EDGE,"E12"),sQuery(id+"F0.wireOp",EDGE,"E13"),sQuery(id+"F0.wireOp",EDGE,"E14"),sQuery(id+"F0.wireOp",EDGE,"E15"),sQuery(id+"F0.wireOp",EDGE,"E17.filletArc"),sQuery(id+"F0.wireOp",EDGE,"E18.filletArc"),sQuery(id+"F0.wireOp",EDGE,"E19.filletArc"),sQuery(id+"F0.wireOp",EDGE,"E20.filletArc"),sQuery(id+"F0.wireOp",EDGE,"E25.0"),sQuery(id+"F0.wireOp",EDGE,"E25.1"),sQuery(id+"F0.wireOp",EDGE,"E25.2"),sQuery(id+"F0.wireOp",EDGE,"E25.3"),sQuery(id+"F0.wireOp",EDGE,"E25.4"),sQuery(id+"F0.wireOp",EDGE,"E25.5"),sQuery(id+"F0.wireOp",EDGE,"E25.6"),sQuery(id+"F0.wireOp",EDGE,"E25.7")])],"isStart":false});
            extrude(context, id + "F17", {"entities" : qUnion([Q0]), "endBound" : BoundingType.UP_TO_SURFACE, "endBoundEntityFace" : qUnion([Q1]), "depth" : 25 * mm});
        }
    });
